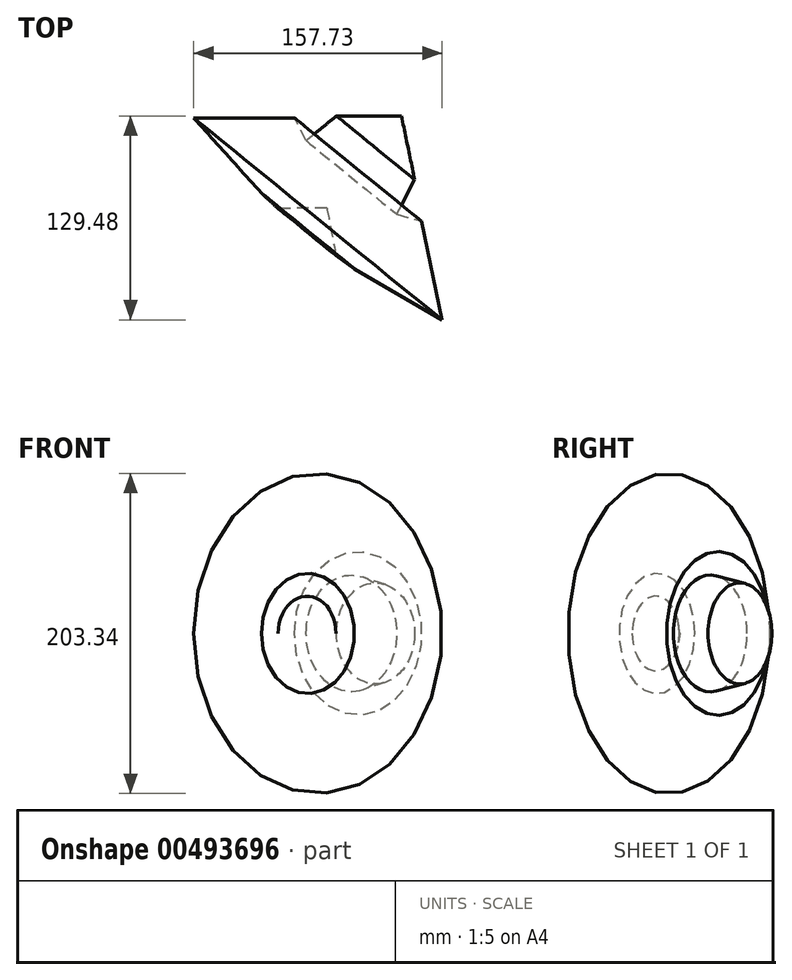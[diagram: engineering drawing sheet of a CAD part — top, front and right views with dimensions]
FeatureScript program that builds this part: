
annotation { "Feature Type Name" : "Feature", "Feature Type Description" : "" }
export const myFeature = defineFeature(function(context is Context, id is Id, definition is map)
    precondition{}
    {
        {
            var Q0;
            Q0=qCreatedBy(makeId("Top.planeOp"),FACE);
            var sketch = newSketch(context, id + "F0", { "sketchPlane" : qUnion([Q0])});
            skLineSegment(sketch, "E0", {"start": v(-64, 39.02) * mm, "end": v(0, 39.02) * mm});
            skLineSegment(sketch, "E1", {"start": v(0, 39.02) * mm, "end": v(7.5, 24.52) * mm});
            skLineSegment(sketch, "E2", {"start": v(7.5, 24.52) * mm, "end": v(26.65, 40.19) * mm});
            skLineSegment(sketch, "E3", {"start": v(26.65, 40.19) * mm, "end": v(68, 40.19) * mm});
            skLineSegment(sketch, "E4", {"start": v(-64, 39.02) * mm, "end": v(-19.92, -9.87) * mm});
            skLineSegment(sketch, "E5", {"start": v(68, 40.19) * mm, "end": v(20.55, -18.14) * mm});
            skLineSegment(sketch, "E6", {"start": v(-22.54, -7.25) * mm, "end": v(-10.35, -18.57) * mm});
            skLineSegment(sketch, "E7", {"start": v(-10.35, -18.57) * mm, "end": v(20.55, -18.14) * mm});
            skSolve(sketch);
        }
        {
            var Q0;
            {var subQ0=sQuery(id+"F0.wireOp",EDGE,"E0");Q0=makeQuery(id+"F0.imprint","IMPRINT",FACE,{"disambiguationData":[TD([[makeQuery(id+"F0.imprint","IMPRINT",EDGE,{"derivedFrom":subQ0}),-1.0]])]});}
            var Q1;
            Q1=sQuery(id+"F0.wireOp",EDGE,"E5");
            revolve(context, id + "F1", {"entities" : qUnion([Q0]), "axis" : qUnion([Q1]), "revolveType" : RevolveType.FULL});
        }
    });
